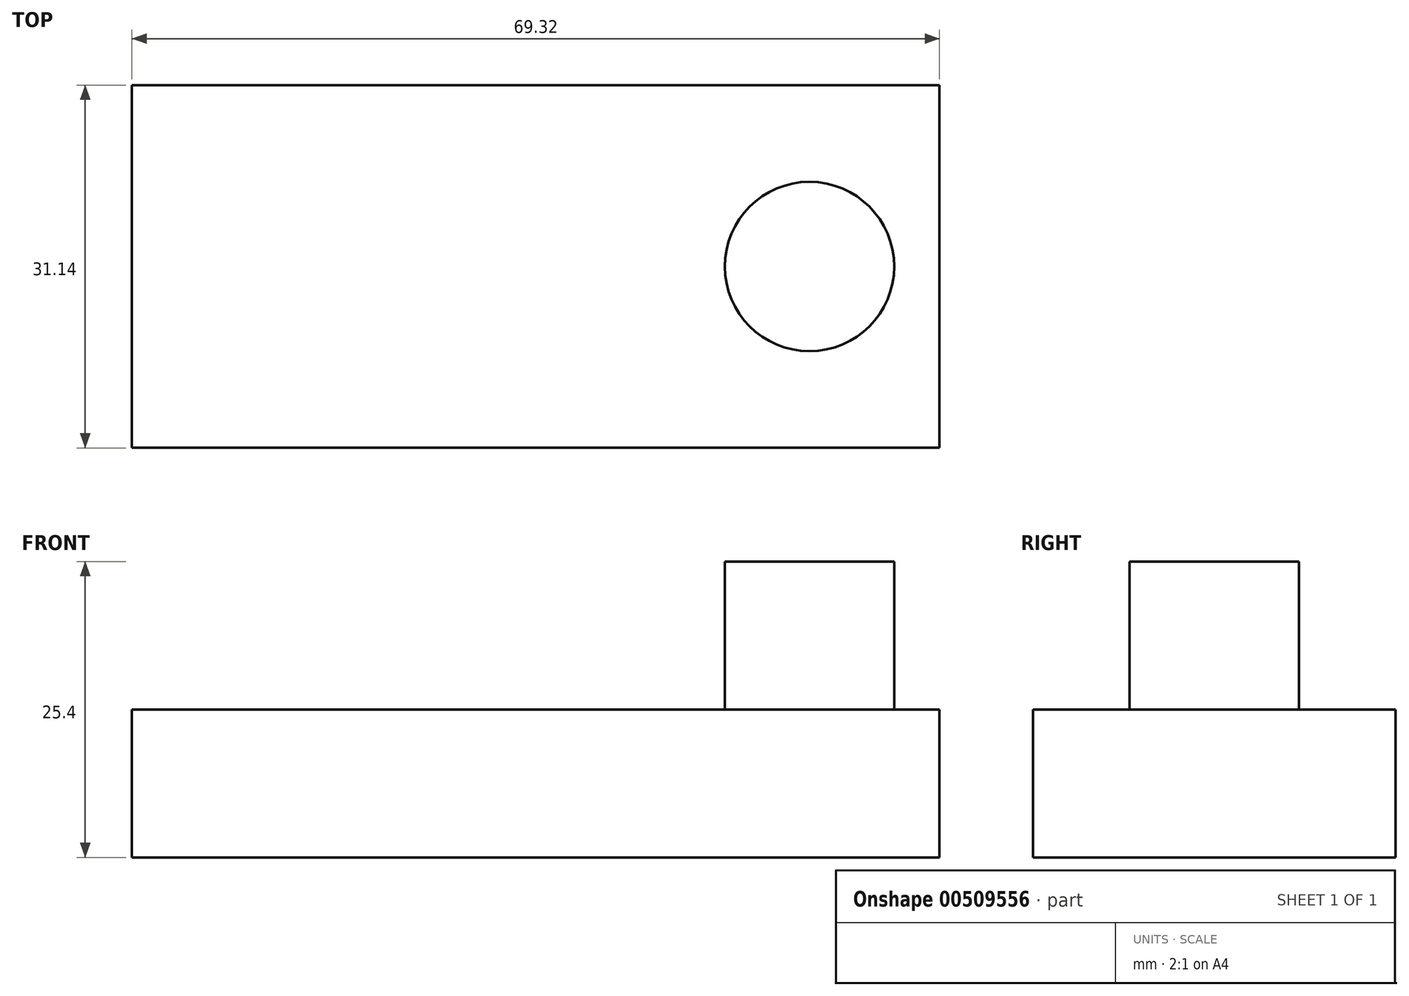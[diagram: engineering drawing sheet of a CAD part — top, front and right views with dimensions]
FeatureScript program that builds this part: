
annotation { "Feature Type Name" : "Feature", "Feature Type Description" : "" }
export const myFeature = defineFeature(function(context is Context, id is Id, definition is map)
    precondition{}
    {
        {
            var Q0;
            Q0=qCreatedBy(makeId("Top.planeOp"),FACE);
            var sketch = newSketch(context, id + "F0", { "sketchPlane" : qUnion([Q0])});
            skLineSegment(sketch, "E0.bottom", {"start": v(34.66, 15.57) * mm, "end": v(-34.66, 15.57) * mm});
            skLineSegment(sketch, "E0.top", {"start": v(34.66, -15.57) * mm, "end": v(-34.66, -15.57) * mm});
            skLineSegment(sketch, "E0.left", {"start": v(34.66, 15.57) * mm, "end": v(34.66, -15.57) * mm});
            skLineSegment(sketch, "E0.right", {"start": v(-34.66, 15.57) * mm, "end": v(-34.66, -15.57) * mm});
            skPoint(sketch, "E0.middle", {"position": v(0, 0) * mm});
            skCircle(sketch, "E1", {"center": v(23.5, 0) * mm, "radius": 7.27 * mm});
            skSolve(sketch);
        }
        {
            var Q0;
            Q0=makeQuery(id+"F0.imprint","IMPRINT",FACE,{"disambiguationData":[TD([[makeQuery(id+"F0.imprint","IMPRINT",EDGE,{"derivedFrom":sQuery(id+"F0.wireOp",EDGE,"E1")}),1.0]])]});
            extrude(context, id + "F1", {"entities" : qUnion([Q0]), "depth" : 25.4 * mm});
        }
        {
            var Q0;
            Q0=makeQuery(id+"F0.imprint","IMPRINT",FACE,{"disambiguationData":[TD([[makeQuery(id+"F0.imprint","IMPRINT",EDGE,{"derivedFrom":sQuery(id+"F0.wireOp",EDGE,"E0.bottom")}),1.0]])]});
            extrude(context, id + "F2", {"entities" : qUnion([Q0]), "operationType" : NewBodyOperationType.ADD, "depth" : 12.7 * mm});
        }
    });
